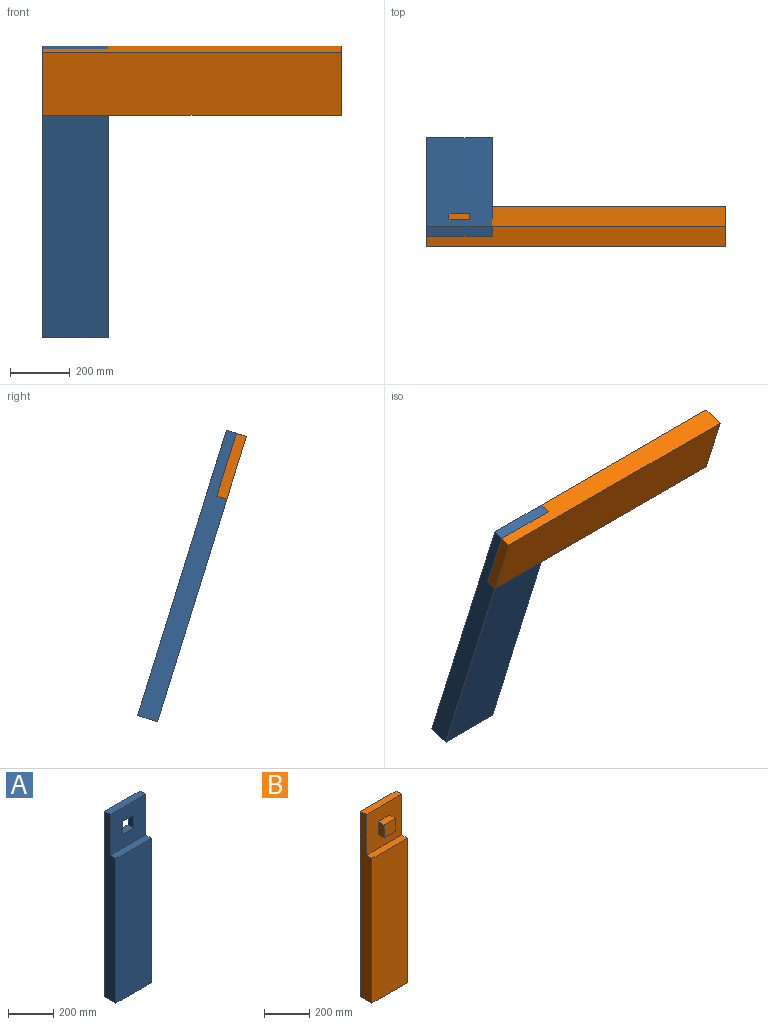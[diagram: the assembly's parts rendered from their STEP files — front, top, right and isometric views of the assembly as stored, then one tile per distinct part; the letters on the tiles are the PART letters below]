
ASSEMBLY  parts=2 mates=1
PART A: 12 faces, bbox 220x70x1000 mm
  f0: plane 220x220mm, normal (0,-1,0), area 43500mm2, adj f3,f4,f5,f6,f8,f9,f10,f11
  f1: plane 1000x220mm, normal (0,1,0), area 215100mm2, adj f2,f3,f4,f5,f8,f9,f10,f11
  f2: plane 220x70mm, normal (0,0,-1), area 15400mm2, adj f1,f3,f5,f7
  f3: plane 1000x70mm, normal (1,0,0), area 62300mm2, adj f0,f1,f2,f4,f6,f7
  f4: plane 220x35mm, normal (0,0,1), area 7700mm2, adj f0,f1,f3,f5
  f5: plane 1000x70mm, normal (-1,0,0), area 62300mm2, adj f0,f1,f2,f4,f6,f7
  f6: plane 220x35mm, normal (0,0,1), area 7700mm2, adj f0,f3,f5,f7
  f7: plane 780x220mm, normal (0,-1,0), area 171600mm2, adj f2,f3,f5,f6
  f8: plane 70x35mm, normal (0,0,-1), area 2450mm2, adj f0,f1,f9,f11
  f9: plane 70x35mm, normal (1,0,0), area 2450mm2, adj f0,f1,f8,f10
  f10: plane 70x35mm, normal (0,0,1), area 2450mm2, adj f0,f1,f9,f11
  f11: plane 70x35mm, normal (-1,0,0), area 2450mm2, adj f0,f1,f8,f10
PART B: 13 faces, bbox 220x70x1000 mm
  f0: plane 220x70mm, normal (0,0,-1), area 15400mm2, adj f1,f3,f5,f7
  f1: plane 1000x70mm, normal (1,0,0), area 62300mm2, adj f0,f2,f4,f5,f6,f7
  f2: plane 220x35mm, normal (0,0,1), area 7700mm2, adj f1,f3,f4,f5
  f3: plane 1000x70mm, normal (-1,0,0), area 62300mm2, adj f0,f2,f4,f5,f6,f7
  f4: plane 220x220mm, normal (0,-1,0), area 43500mm2, adj f1,f2,f3,f6,f8,f9,f10,f11
  f5: plane 1000x220mm, normal (0,1,0), area 220000mm2, adj f0,f1,f2,f3
  f6: plane 220x35mm, normal (0,0,1), area 7700mm2, adj f1,f3,f4,f7
  f7: plane 780x220mm, normal (0,-1,0), area 171600mm2, adj f0,f1,f3,f6
  f8: plane 70x35mm, normal (0,0,1), area 2450mm2, adj f4,f9,f11,f12
  f9: plane 70x35mm, normal (-1,0,0), area 2450mm2, adj f4,f8,f10,f12
  f10: plane 70x35mm, normal (0,0,-1), area 2450mm2, adj f4,f9,f11,f12
  f11: plane 70x35mm, normal (1,0,0), area 2450mm2, adj f4,f8,f10,f12
  f12: plane 70x70mm, normal (0,-1,0), area 4900mm2, adj f8,f9,f10,f11
PLACE A rot(axis=(1,0,0),17.3deg) t=(149.93,313.84,345.5)mm
PLACE B rot(axis=(-0.7,-0.11,0.7),167.8deg) t=(929.93,15.33,1069.51)mm
MATE planar B.f4 <-> A.f0  axis (0,0.95,0.3) through (-70.07,-16.6,1289.97)mm
